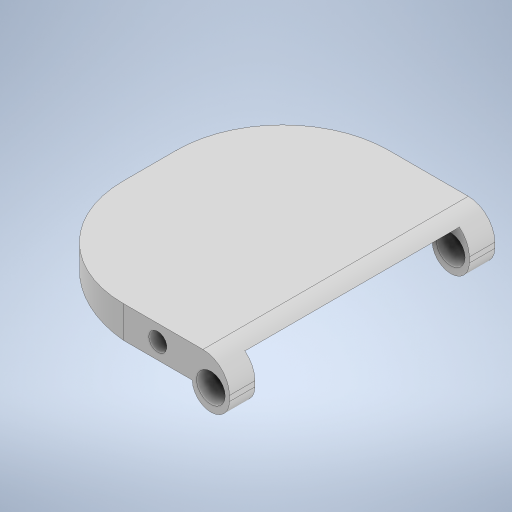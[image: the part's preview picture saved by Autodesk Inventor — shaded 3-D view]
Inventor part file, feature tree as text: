
AUTODESK INVENTOR PART (.ipt)
format: ipt  version: 2023 (Build 270158000, 158)  size: 322,560 bytes
history: native  units: in
note: dims shown in document units (in); Inventor stores cm internally (conversion verified against a paired STEP export)
features: thicken_offset x5, sketch x5, extrude x4, fillet x2, chamfer x2, hole x1
ambient origin geometry x8: Origin, YZ Plane, XZ Plane, XY Plane, X Axis, Y Axis, Z Axis, Center Point
bodies: Solid1 (feature_tree)
feature tree (19):
  extrude  "Extrusion1"  Depth=0.1969in
  extrude  "Extrusion2"  Depth=1.9685in TaperAngle=0.0deg
  fillet  "Fillet1"  Radius=0.0394in
  hole  "Hole1"  [1 undecoded]
  extrude  "Extrusion3"  Depth=1.5748in TaperAngle=0.0deg
  chamfer  "Chamfer4"  Distance=0.3937in
  chamfer  "Chamfer5"  Distance=1.5748in
  fillet  "Fillet6"  Radius=0.1575in
  extrude  "Extrusion4"  Depth=0.3937in TaperAngle=0.0deg
  thicken_offset  "Thicken1"
  thicken_offset  "Thicken2"
  thicken_offset  "Thicken3"
  thicken_offset  "Thicken4"
  thicken_offset  "Thicken5"
  sketch  "Sketch1"  dims[d0=0.2756in d2=0.1969in]
  sketch  "Sketch2"  dims[d3=0.1575in d5=1.9685in d6=0.0in d8=0.0394in]
  sketch  "Sketch3"  dims[d9=0.1575in d10=1.5748in]
  sketch  "Sketch4"  dims[d11=0.2362in d12=1.5748in d13=0.0in]
  sketch  "Sketch5"  dims[d14=0.1969in d15=0.3937in d16=0.1181in d17=0.2362in d18=0.1575in d19=0.0787in d20=90.0deg d21=0.0787in d22=0.0in d23=1.5748in d24=0.1575in d25=0.3543in d26=0.0in d40=0.1181in d41=0.7874in d42=0.0787in d43=45.0deg d44=0.7874in d45=0.0787in d46=45.0deg d47=0.7874in d48=0.0787in d49=0.3937in d50=0.0in d51=0.0079in d52=0.0079in d53=0.0079in d54=0.0079in d55=0.0079in d56=0.0079in d57=0.0079in d58=0.0079in d59=0.0079in d60=0.0079in]
note: 1 required parameter value undecoded (feature->parameter linkage not recoverable at this tier; creation-order binding heuristic only, values carry confidence <= 0.55)
